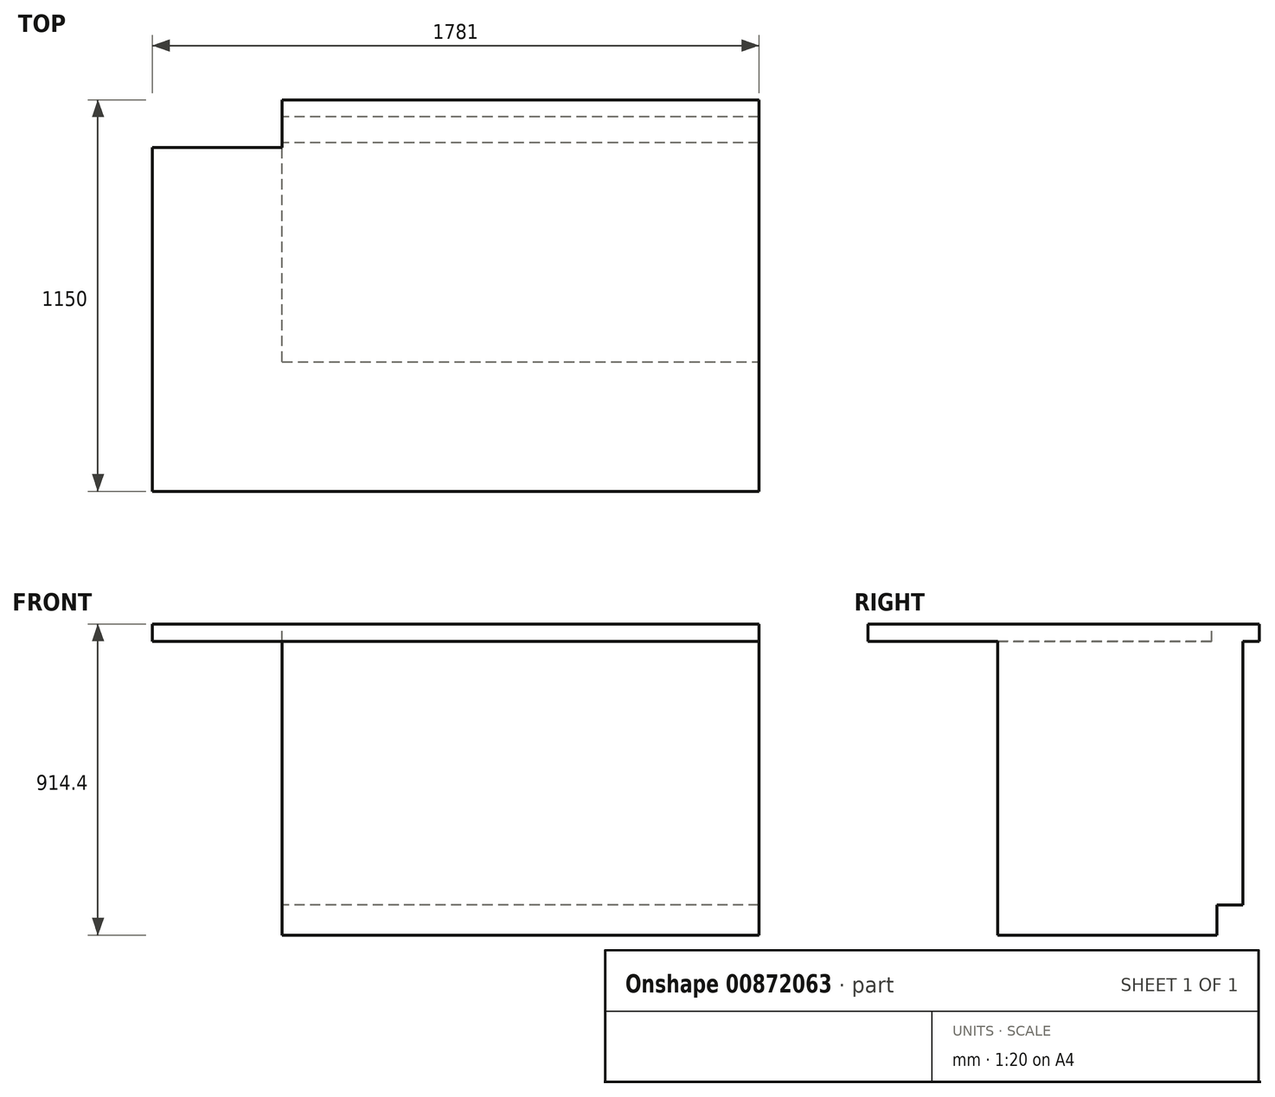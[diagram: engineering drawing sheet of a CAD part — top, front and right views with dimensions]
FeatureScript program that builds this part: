
annotation { "Feature Type Name" : "Feature", "Feature Type Description" : "" }
export const myFeature = defineFeature(function(context is Context, id is Id, definition is map)
    precondition{}
    {
        {
            var Q0;
            Q0=qCreatedBy(makeId("Top.planeOp"),FACE);
            var sketch = newSketch(context, id + "F0", { "sketchPlane" : qUnion([Q0])});
            skLineSegment(sketch, "E0.bottom", {"start": v(0, 0) * mm, "end": v(1400, 0) * mm});
            skLineSegment(sketch, "E0.top", {"start": v(0, 720) * mm, "end": v(1400, 720) * mm});
            skLineSegment(sketch, "E0.left", {"start": v(0, 0) * mm, "end": v(0, 720) * mm});
            skLineSegment(sketch, "E0.right", {"start": v(1400, 0) * mm, "end": v(1400, 720) * mm});
            skSolve(sketch);
        }
        {
            var Q0;
            Q0=makeQuery(id+"F0.imprint","IMPRINT",FACE,{"disambiguationData":[TD([[makeQuery(id+"F0.imprint","IMPRINT",EDGE,{"derivedFrom":sQuery(id+"F0.wireOp",EDGE,"E0.bottom")}),1.0]])]});
            extrude(context, id + "F1", {"entities" : qUnion([Q0]), "depth" : 863.6 * mm, "offsetDistance" : 25 * mm});
        }
        {
            var Q0;
            Q0=qCreatedBy(makeId("Right.planeOp"),FACE);
            var sketch = newSketch(context, id + "F2", { "sketchPlane" : qUnion([Q0])});
            skLineSegment(sketch, "E1.0", {"start": v(0, 0) * mm, "end": v(720, 0) * mm, "construction": true});
            skLineSegment(sketch, "E2.0", {"start": v(720, 863.6) * mm, "end": v(720, 0) * mm, "construction": true});
            skLineSegment(sketch, "E3.0", {"start": v(0, 863.6) * mm, "end": v(0, 0) * mm, "construction": true});
            skLineSegment(sketch, "E4.bottom", {"start": v(720, 0) * mm, "end": v(643.8, 0) * mm});
            skLineSegment(sketch, "E4.top", {"start": v(720, 88.9) * mm, "end": v(643.8, 88.9) * mm});
            skLineSegment(sketch, "E4.left", {"start": v(720, 0) * mm, "end": v(720, 88.9) * mm});
            skLineSegment(sketch, "E4.right", {"start": v(643.8, 0) * mm, "end": v(643.8, 88.9) * mm});
            skSolve(sketch);
        }
        {
            var Q0;
            Q0 = qSketchRegion(id + "F2", true);
            extrude(context, id + "F3", {"entities" : qUnion([Q0]), "operationType" : NewBodyOperationType.REMOVE, "endBound" : BoundingType.THROUGH_ALL, "depth" : 25 * mm, "offsetDistance" : 25 * mm});
        }
        {
            var Q0;
            Q0=qCreatedBy(makeId("Right.planeOp"),FACE);
            var sketch = newSketch(context, id + "F4", { "sketchPlane" : qUnion([Q0])});
            skLineSegment(sketch, "E5.0", {"start": v(0, 863.6) * mm, "end": v(720, 863.6) * mm, "construction": true});
            skLineSegment(sketch, "E6.bottom", {"start": v(769, 863.6) * mm, "end": v(-381, 863.6) * mm});
            skLineSegment(sketch, "E6.top", {"start": v(769, 914.4) * mm, "end": v(-381, 914.4) * mm});
            skLineSegment(sketch, "E6.left", {"start": v(769, 863.6) * mm, "end": v(769, 914.4) * mm});
            skLineSegment(sketch, "E6.right", {"start": v(-381, 863.6) * mm, "end": v(-381, 914.4) * mm});
            skSolve(sketch);
        }
        {
            var Q0;
            Q0=makeQuery(id+"F4.imprint","IMPRINT",FACE,{"disambiguationData":[TD([[makeQuery(id+"F4.imprint","IMPRINT",EDGE,{"derivedFrom":sQuery(id+"F4.wireOp",EDGE,"E6.bottom")}),-1.0]])]});
            var Q1;
            Q1=makeQuery(id+"F1.opExtrude","SWEPT_FACE",FACE,{"disambiguationData":[OSD([sQuery(id+"F0.wireOp",EDGE,"E0.right")])]});
            extrude(context, id + "F5", {"entities" : qUnion([Q0]), "endBound" : BoundingType.UP_TO_SURFACE, "depth" : 25 * mm, "endBoundEntityFace" : qUnion([Q1]), "offsetDistance" : 25 * mm});
        }
        {
            var Q0;
            Q0=makeQuery(id+"F5.opExtrude","CAP_FACE",FACE,{"disambiguationData":[OSD([sQuery(id+"F4.wireOp",EDGE,"E6.bottom"),sQuery(id+"F4.wireOp",EDGE,"E6.top"),sQuery(id+"F4.wireOp",EDGE,"E6.left"),sQuery(id+"F4.wireOp",EDGE,"E6.right")])],"isStart":true});
            extrude(context, id + "F6", {"entities" : qUnion([Q0]), "operationType" : NewBodyOperationType.ADD, "depth" : 381 * mm, "offsetDistance" : 25 * mm});
        }
        {
            var Q0;
            {var subQ0=sQuery(id+"F4.wireOp",EDGE,"E6.top");Q0=makeQuery(id+"F6.boolean.opBoolean","MERGE",FACE,{"derivedFrom":[makeQuery(id+"F5.opExtrude","SWEPT_FACE",FACE,{"disambiguationData":[OSD([subQ0])]}),makeQuery(id+"F6.opExtrude","SWEPT_FACE",FACE,{"disambiguationData":[OSD([subQ0])]})]});}
            var sketch = newSketch(context, id + "F7", { "sketchPlane" : qUnion([Q0])});
            skPoint(sketch, "E7.0", {"position": v(-381, 769) * mm});
            skLineSegment(sketch, "E8.bottom", {"start": v(-381, 769) * mm, "end": v(0, 769) * mm});
            skLineSegment(sketch, "E8.top", {"start": v(-381, 629) * mm, "end": v(0, 629) * mm});
            skLineSegment(sketch, "E8.left", {"start": v(-381, 769) * mm, "end": v(-381, 629) * mm});
            skLineSegment(sketch, "E8.right", {"start": v(0, 769) * mm, "end": v(0, 629) * mm});
            skSolve(sketch);
        }
        {
            var Q0;
            Q0 = qSketchRegion(id + "F7", true);
            var Q1;
            {var subQ0=sQuery(id+"F4.wireOp",EDGE,"E6.bottom");Q1=makeQuery(id+"F6.boolean.opBoolean","MERGE",FACE,{"derivedFrom":[makeQuery(id+"F5.opExtrude","SWEPT_FACE",FACE,{"disambiguationData":[OSD([subQ0])]}),makeQuery(id+"F6.opExtrude","SWEPT_FACE",FACE,{"disambiguationData":[OSD([subQ0])]})]});}
            extrude(context, id + "F8", {"entities" : qUnion([Q0]), "operationType" : NewBodyOperationType.REMOVE, "endBound" : BoundingType.UP_TO_SURFACE, "oppositeDirection" : true, "depth" : 25 * mm, "endBoundEntityFace" : qUnion([Q1]), "offsetDistance" : 25 * mm});
        }
    });
